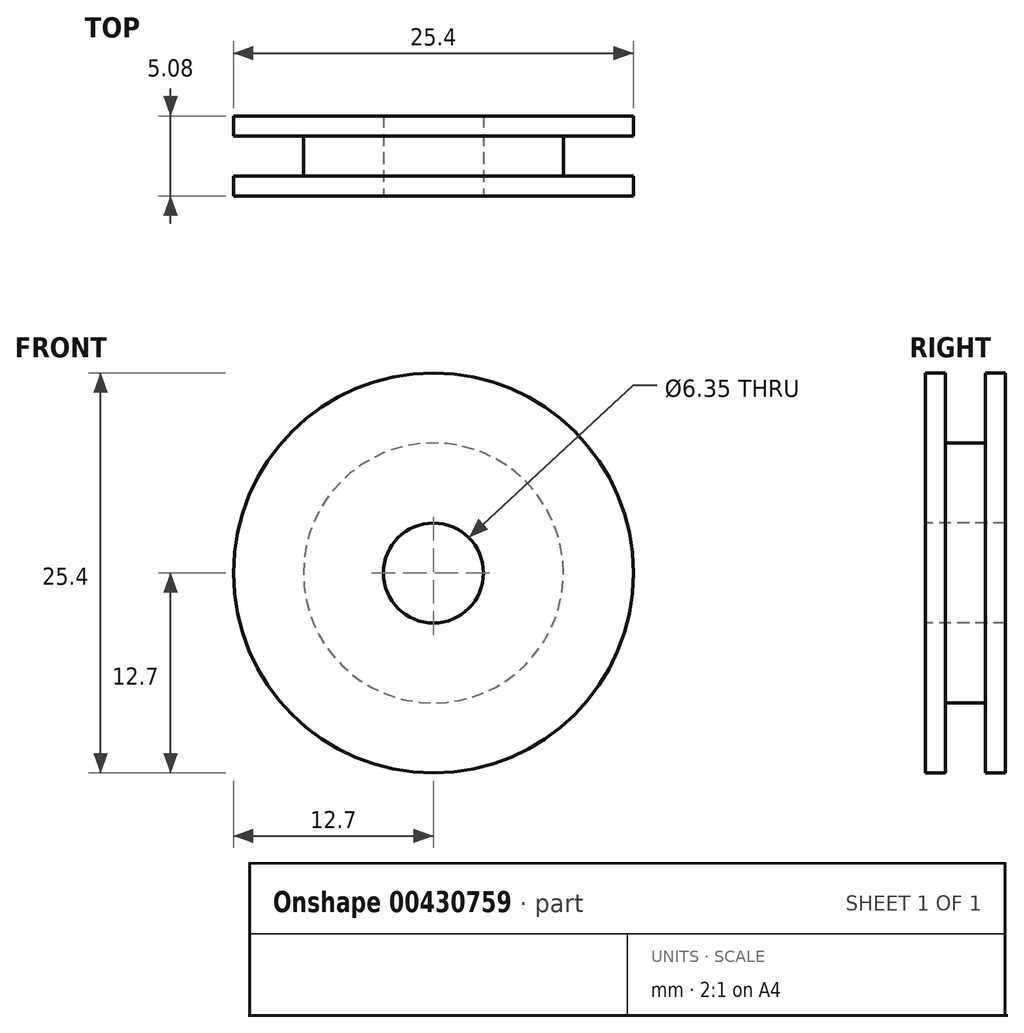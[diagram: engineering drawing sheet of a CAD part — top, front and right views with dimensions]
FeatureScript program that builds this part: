
annotation { "Feature Type Name" : "Feature", "Feature Type Description" : "" }
export const myFeature = defineFeature(function(context is Context, id is Id, definition is map)
    precondition{}
    {
        {
            var Q0;
            Q0=qCreatedBy(makeId("Front.planeOp"),FACE);
            var sketch = newSketch(context, id + "F0", { "sketchPlane" : qUnion([Q0])});
            skCircle(sketch, "E0", {"center": v(0, 0) * mm, "radius": 12.7 * mm});
            skSolve(sketch);
        }
        {
            var Q0;
            Q0 = qSketchRegion(id + "F0", true);
            extrude(context, id + "F1", {"entities" : qUnion([Q0]), "depth" : 1.27 * mm});
        }
        {
            var Q0;
            Q0=makeQuery(id+"F1.opExtrude","CAP_FACE",FACE,{"disambiguationData":[OSD([sQuery(id+"F0.wireOp",EDGE,"E0")])],"isStart":false});
            var sketch = newSketch(context, id + "F2", { "sketchPlane" : qUnion([Q0])});
            skCircle(sketch, "E1", {"center": v(0, 0) * mm, "radius": 8.26 * mm});
            skSolve(sketch);
        }
        {
            var Q0;
            Q0=makeQuery(id+"F2.imprint","IMPRINT",FACE,{"disambiguationData":[TD([[makeQuery(id+"F2.imprint","IMPRINT",EDGE,{"derivedFrom":sQuery(id+"F2.wireOp",EDGE,"E1")}),1.0]])]});
            extrude(context, id + "F3", {"entities" : qUnion([Q0]), "operationType" : NewBodyOperationType.ADD, "depth" : 2.54 * mm});
        }
        {
            var Q0;
            Q0=makeQuery(id+"F3.opExtrude","CAP_FACE",FACE,{"disambiguationData":[OSD([sQuery(id+"F2.wireOp",EDGE,"E1")])],"isStart":false});
            var sketch = newSketch(context, id + "F4", { "sketchPlane" : qUnion([Q0])});
            skCircle(sketch, "E2", {"center": v(0, 0) * mm, "radius": 12.7 * mm});
            skSolve(sketch);
        }
        {
            var Q0;
            Q0 = qSketchRegion(id + "F4", true);
            extrude(context, id + "F5", {"entities" : qUnion([Q0]), "operationType" : NewBodyOperationType.ADD, "depth" : 1.27 * mm});
        }
        {
            var Q0;
            Q0=makeQuery(id+"F5.opExtrude","CAP_FACE",FACE,{"disambiguationData":[OSD([sQuery(id+"F4.wireOp",EDGE,"E2")])],"isStart":false});
            var sketch = newSketch(context, id + "F6", { "sketchPlane" : qUnion([Q0])});
            skCircle(sketch, "E3", {"center": v(0, 0) * mm, "radius": 3.18 * mm});
            skSolve(sketch);
        }
        {
            var Q0;
            Q0 = qSketchRegion(id + "F6", true);
            extrude(context, id + "F7", {"entities" : qUnion([Q0]), "operationType" : NewBodyOperationType.REMOVE, "oppositeDirection" : true, "depth" : 25.4 * mm});
        }
    });
